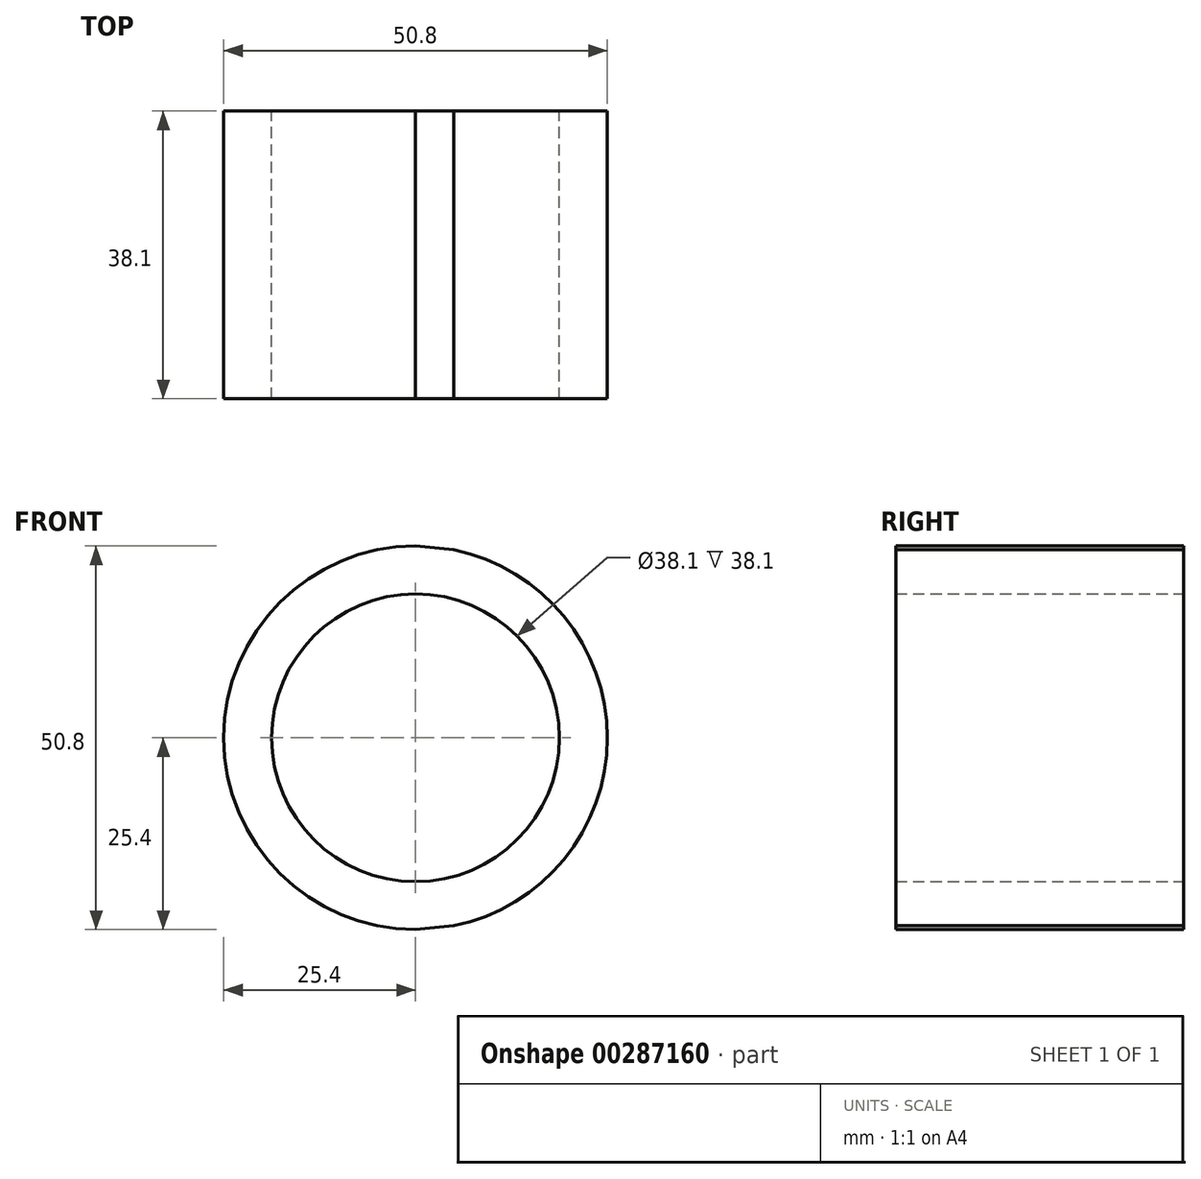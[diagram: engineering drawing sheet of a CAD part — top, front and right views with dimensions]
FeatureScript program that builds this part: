
annotation { "Feature Type Name" : "Feature", "Feature Type Description" : "" }
export const myFeature = defineFeature(function(context is Context, id is Id, definition is map)
    precondition{}
    {
        {
            var Q0;
            Q0=qCreatedBy(makeId("Front.planeOp"),FACE);
            var sketch = newSketch(context, id + "F0", { "sketchPlane" : qUnion([Q0])});
            skArc(sketch, "E0", {"start": v(0, -6.35) * mm, "mid": v(6.35, 0) * mm, "end": v(0, 6.35) * mm});
            skArc(sketch, "E1", {"start": v(-50.8, 6.35) * mm, "mid": v(-57.15, 0) * mm, "end": v(-50.8, -6.35) * mm});
            skCircle(sketch, "E2", {"center": v(-88.9, 0) * mm, "radius": 19.05 * mm});
            skCircle(sketch, "E3", {"center": v(-88.9, 0) * mm, "radius": 25.4 * mm});
            skCircle(sketch, "E4", {"center": v(38.1, 0) * mm, "radius": 6.35 * mm});
            skCircle(sketch, "E5", {"center": v(38.1, 0) * mm, "radius": 12.7 * mm});
            skPoint(sketch, "E6", {"position": v(-50.8, 6.35) * mm});
            skPoint(sketch, "E7", {"position": v(-50.8, -6.35) * mm});
            skPoint(sketch, "E8", {"position": v(0, 6.35) * mm});
            skPoint(sketch, "E9", {"position": v(0, -6.35) * mm});
            skLineSegment(sketch, "E10", {"start": v(-50.8, -6.35) * mm, "end": v(0, -6.35) * mm});
            skLineSegment(sketch, "E11", {"start": v(-50.8, 6.35) * mm, "end": v(0, 6.35) * mm});
            skLineSegment(sketch, "E12", {"start": v(-88.9, 25.4) * mm, "end": v(38.1, 12.7) * mm});
            skLineSegment(sketch, "E13", {"start": v(-88.9, -25.4) * mm, "end": v(38.1, -12.7) * mm});
            skSolve(sketch);
        }
        {
            var Q0;
            Q0=makeQuery(id+"F0.imprint","IMPRINT",FACE,{"disambiguationData":[TD([[makeQuery(id+"F0.imprint","IMPRINT",EDGE,{"derivedFrom":sQuery(id+"F0.wireOp",EDGE,"E2")}),-1.0]])]});
            extrude(context, id + "F1", {"entities" : qUnion([Q0]), "depth" : 38.1 * mm});
        }
    });
